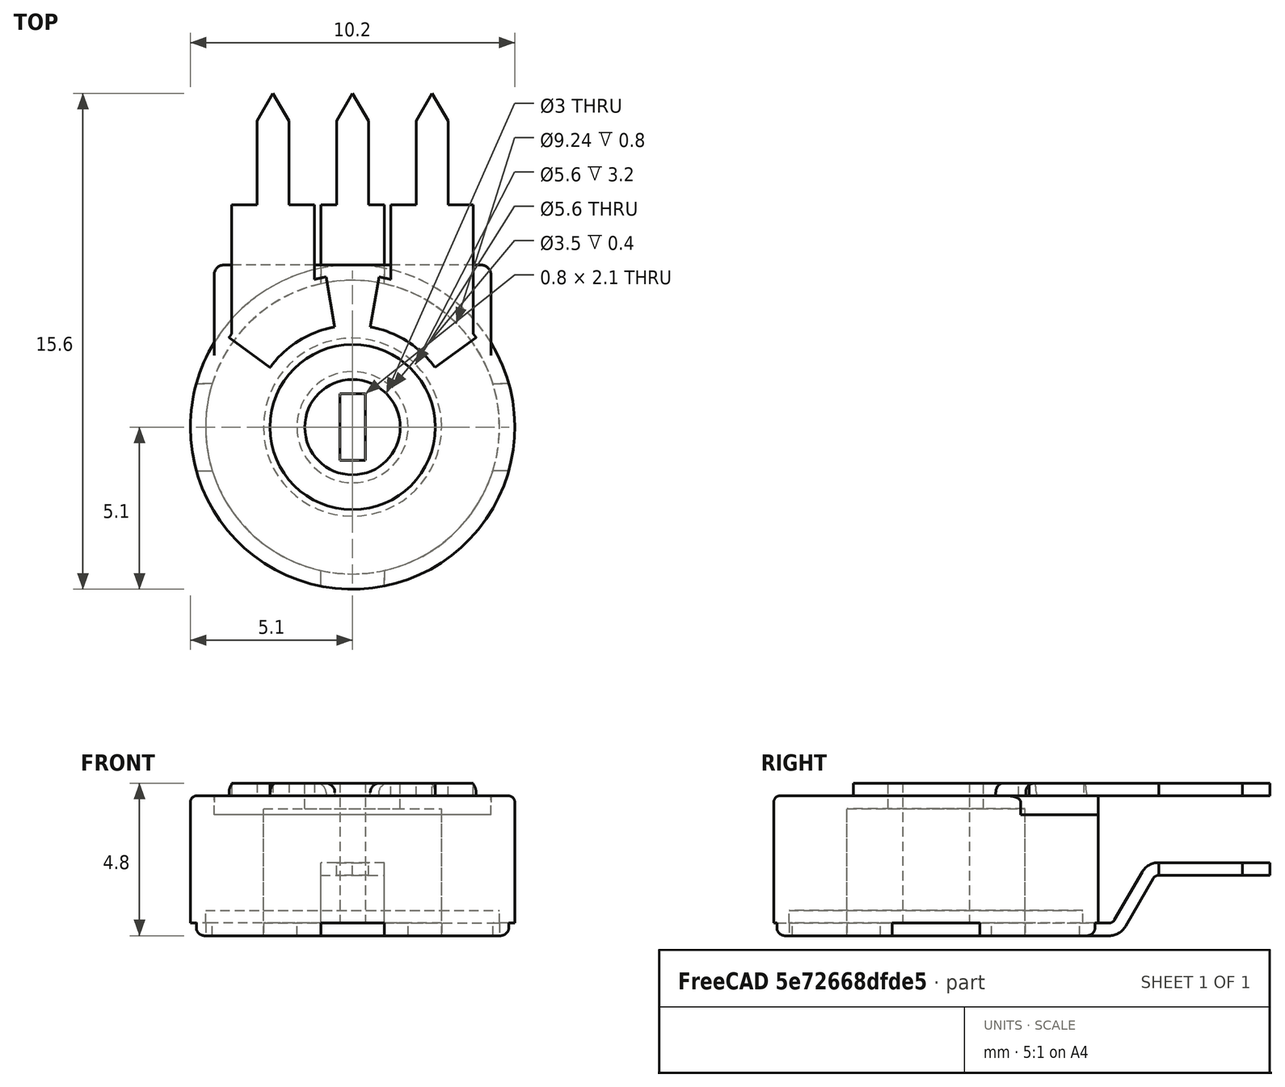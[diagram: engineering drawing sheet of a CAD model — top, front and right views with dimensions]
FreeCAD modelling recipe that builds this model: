
FCSTD DOCUMENT  (FreeCAD 0.16R6703 (Git))
Label: Assembly
License: CreativeCommons Attribution-ShareAlike
LicenseURL: http://creativecommons.org/licenses/by-sa/4.0/
objects: Part::Feature×5, Part::Fillet×2, Part::Compound×1
note: 8 computed .brp shape members not serialized (recipe doc carries the construction recipe); baked Part::Feature solids carry a one-line shape summary decoded from their .brp

FEATURE [Part::Feature] Cut001  label="Rotor"
  shape: bbox 5.6 x 5.6 x 4.8 mm, 11 faces (baked)
FEATURE [Part::Feature] Common001  label="S"
  Placement = pos=(0,0,0.4) rot=(0.707107,0.707107,0;3.14159rad)
  shape: bbox 9.24 x 15.12 x 2.3 mm, 20 faces (baked)
FEATURE [Part::Feature] Pad003  label="A"
  Placement = pos=(0,10.5,4.4) rot=(0,0,1;3.14159rad)
  shape: bbox 3.328 x 8.619 x 0.4 mm, 15 faces (baked)
FEATURE [Part::Feature] Pad001  label="E"
  Placement = pos=(0,10.5,4.8) rot=(1,0,0;3.14159rad)
  shape: bbox 3.328 x 8.619 x 0.4 mm, 15 faces (baked)
FEATURE [Part::Feature] Fillet001001  label="Core"
  Placement = pos=(0,0,0) rot=(0,0,1;3.14159rad)
  shape: bbox 11.04 x 10.93 x 4.8 mm, 37 faces (baked)
FEATURE [Part::Fillet] Fillet
  Base = -> Pad003
  Edges = 2 edges r=0.3: [Edge31,Edge37]
FEATURE [Part::Fillet] Fillet001002
  Base = -> Pad001
  Edges = 2 edges r=0.3: [Edge30,Edge36]
FEATURE [Part::Compound] Compound
  Links = -> [Fillet001002,Fillet,Fillet001001,Common001,Cut001]
